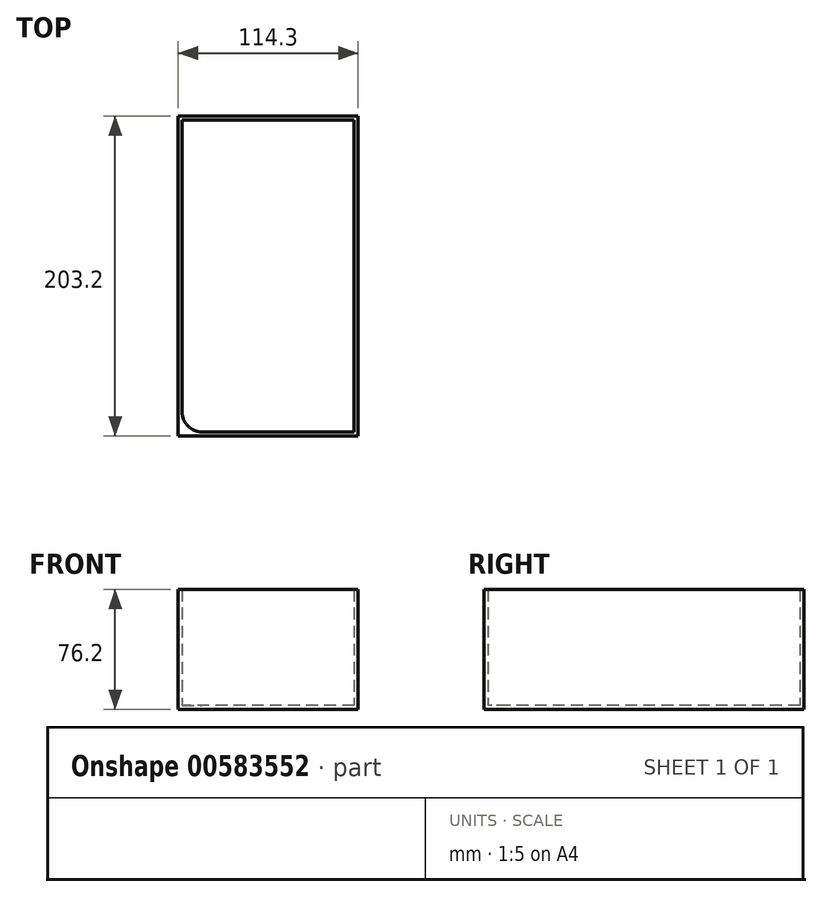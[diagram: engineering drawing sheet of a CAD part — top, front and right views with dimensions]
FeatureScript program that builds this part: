
annotation { "Feature Type Name" : "Feature", "Feature Type Description" : "" }
export const myFeature = defineFeature(function(context is Context, id is Id, definition is map)
    precondition{}
    {
        {
            var Q0;
            Q0=qCreatedBy(makeId("Top.planeOp"),FACE);
            var sketch = newSketch(context, id + "F0", { "sketchPlane" : qUnion([Q0])});
            skLineSegment(sketch, "E0.bottom", {"start": v(46.99, 48.9) * mm, "end": v(-47, 48.9) * mm, "construction": true});
            skLineSegment(sketch, "E0.top", {"start": v(47, -48.9) * mm, "end": v(-46.99, -48.9) * mm, "construction": true});
            skLineSegment(sketch, "E0.left", {"start": v(46.99, 48.9) * mm, "end": v(47, -48.9) * mm, "construction": true});
            skLineSegment(sketch, "E0.right", {"start": v(-47, 48.9) * mm, "end": v(-46.99, -48.9) * mm, "construction": true});
            skPoint(sketch, "E0.middle", {"position": v(0, 0) * mm});
            skLineSegment(sketch, "E1.bottom", {"start": v(57.15, 139.7) * mm, "end": v(-57.15, 139.7) * mm});
            skLineSegment(sketch, "E1.top", {"start": v(57.15, -63.5) * mm, "end": v(-57.15, -63.5) * mm});
            skLineSegment(sketch, "E1.left", {"start": v(57.15, 139.7) * mm, "end": v(57.15, -63.5) * mm});
            skLineSegment(sketch, "E1.right", {"start": v(-57.15, 139.7) * mm, "end": v(-57.15, -63.5) * mm});
            skPoint(sketch, "E1.middle", {"position": v(0, 38.1) * mm});
            skSolve(sketch);
        }
        {
            var Q0;
            Q0 = qSketchRegion(id + "F0", true);
            extrude(context, id + "F1", {"entities" : qUnion([Q0]), "depth" : 76.2 * mm, "offsetDistance" : 25.4 * mm});
        }
        {
            var Q0;
            Q0=makeQuery(id+"F1.opExtrude","CAP_FACE",FACE,{"disambiguationData":[OSD([sQuery(id+"F0.wireOp",EDGE,"E1.bottom"),sQuery(id+"F0.wireOp",EDGE,"E1.top"),sQuery(id+"F0.wireOp",EDGE,"E1.left"),sQuery(id+"F0.wireOp",EDGE,"E1.right")])],"isStart":false});
            shell(context, id + "F2", {"entities" : qUnion([Q0]), "thickness" : 2.54 * mm});
        }
        {
            var Q0;
            Q0=makeQuery(id+"F2.opShell","OFFSET_EDGE",EDGE,{"disambiguationData":[OSD([sQuery(id+"F0.wireOp",EDGE,"E1.top"),sQuery(id+"F0.wireOp",EDGE,"E1.right")])]});
            fillet(context, id + "F3", {"entities" : qUnion([Q0]), "radius" : 12.7 * mm, "tangentPropagation" : true, "allowEdgeOverflow" : false});
        }
    });
